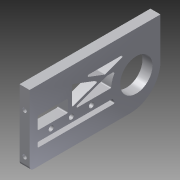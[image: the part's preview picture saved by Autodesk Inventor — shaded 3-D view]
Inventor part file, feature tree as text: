
AUTODESK INVENTOR PART (.ipt)
format: ipt  version: 2015 (Build 190159000, 159)  size: 245,760 bytes
history: native  units: mm
features: sketch x9, extrude x8, projected_geometry x5, reference x3, other x2, fillet x2, pattern_linear x1, hole x1
ambient origin geometry x8: Origin, YZ Plane, XZ Plane, XY Plane, X Axis, Y Axis, Z Axis, Center Point
bodies: Body1 (feature_tree)
feature tree (31):
  other  "Sólido1"
  extrude  "Main Body"  Depth=35.0mm
  extrude  "Bearings"  Depth=20.0mm
  sketch  "Boceto4"  dims[d2=100.0mm d3=0.0mm d11=20.0mm]
  extrude  "Spring_support_space"  Depth=38.0mm
  extrude  "Holes"  Depth=16.1mm
  sketch  "Boceto10"  dims[d30=10.0mm d31=0.0mm d35=2.1mm]
  fillet  "Edges"  Radius=13.0mm
  extrude  "Extrusión6"  Depth=20.0mm
  pattern_linear  "Patrón rectangular1"  Count1=2  [1 undecoded]
  extrude  "Extrusión7"  Depth=35.0mm
  extrude  "Extrusión9"  Depth=10.0mm
  extrude  "Extrusión10"  Depth=15.0mm TaperAngle=0.0deg
  fillet  "Empalme2"  Radius=15.0mm
  hole  "Agujero4"  [1 undecoded]
  sketch  "Boceto1"  dims[d0=5.0mm d1=35.0mm]
  other  "Axles"
  sketch  "Boceto5"  dims[d12=40.0mm d13=38.0mm]
  sketch  "Boceto6"  dims[d14=20.0mm d22=16.1mm d23=13.0mm]
  sketch  "Boceto7"  dims[d24=100.0mm d25=0.0mm d26=20.0mm d27=20.0mm]
  projected_geometry  "Contorno proyectado2"
  sketch  "Boceto8"  dims[d28=35.0mm d29=35.0mm]
  reference  "Referencia1"
  reference  "Referencia2"
  reference  "Referencia3"
  projected_geometry  "Contorno proyectado3"
  projected_geometry  "Contorno proyectado4"
  sketch  "Boceto11"  dims[d36=20.0mm d37=15.0mm d38=0.0mm d39=15.0mm]
  projected_geometry  "Contorno proyectado5"
  projected_geometry  "Contorno proyectado6"
  sketch  "Boceto13"  dims[d41=6.5mm d42=3.0mm d50=2.4mm d51=33.0mm d52=0.0mm d53=50.0mm d55=13.0mm d56=50.0mm d57=10.0mm d58=0.0mm d59=7.0mm d63=2.0mm d64=2.5mm d65=2.5mm d66=2.0mm d67=2.0mm d68=4.0mm d69=25.0mm d70=5.0mm d71=8.0mm d72=1.0mm d74=1.0mm d75=1.0mm d77=2.0mm d78=10.0mm d79=0.0mm d80=0.5mm d81=3.0mm d82=0.0mm d90=2.4mm d91=6.0mm d92=4.6mm d93=2.0mm d94=90.0deg d95=8.0mm d96=20.594885mm]
note: 2 required parameter values undecoded (feature->parameter linkage not recoverable at this tier; creation-order binding heuristic only, values carry confidence <= 0.55)
